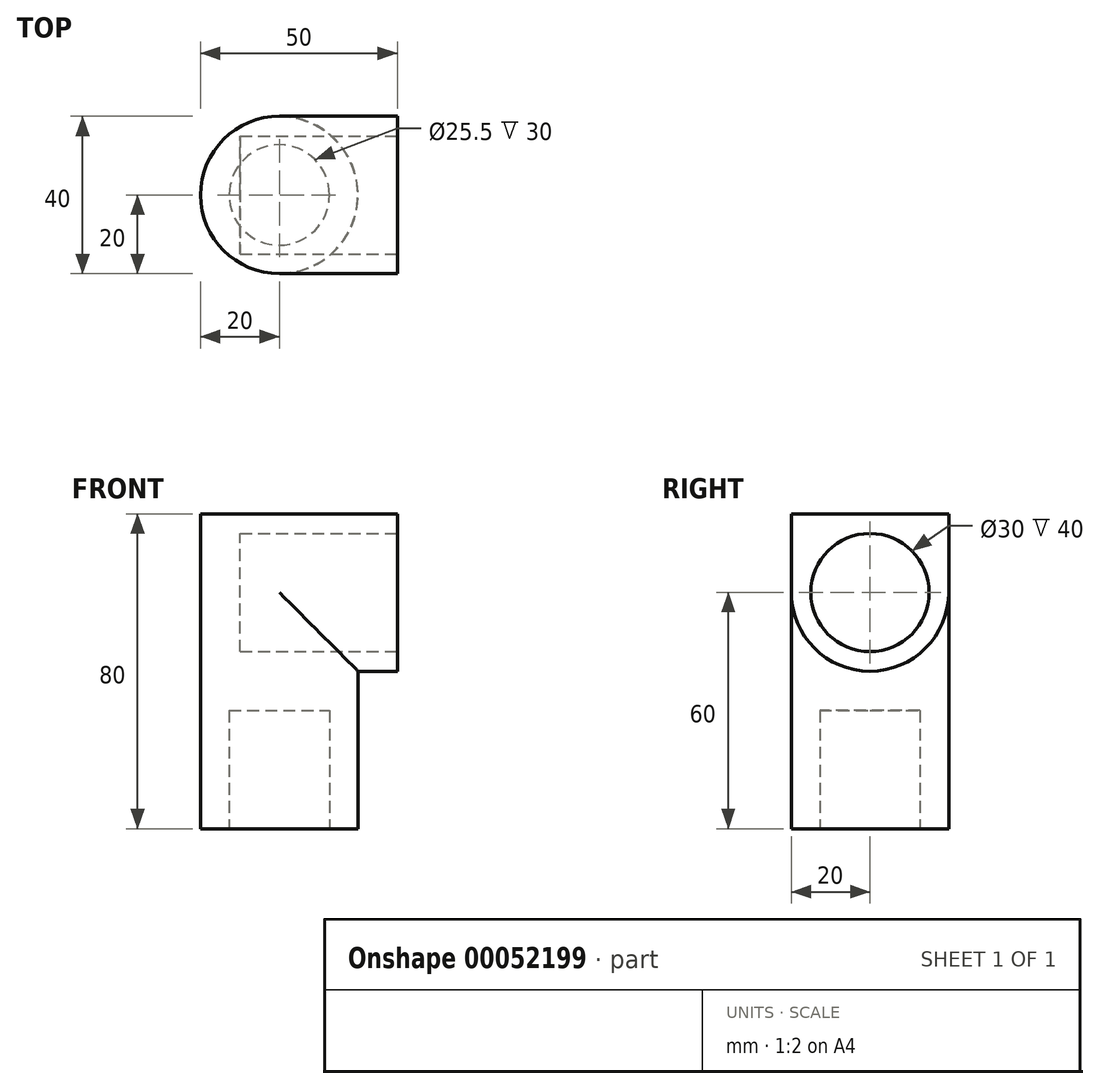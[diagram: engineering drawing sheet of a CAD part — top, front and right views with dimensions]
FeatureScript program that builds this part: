
annotation { "Feature Type Name" : "Feature", "Feature Type Description" : "" }
export const myFeature = defineFeature(function(context is Context, id is Id, definition is map)
    precondition{}
    {
        {
            var Q0;
            Q0=qCreatedBy(makeId("Front.planeOp"),FACE);
            var sketch = newSketch(context, id + "F0", { "sketchPlane" : qUnion([Q0])});
            skLineSegment(sketch, "E0", {"start": v(0, 0) * mm, "end": v(0, -40) * mm});
            skLineSegment(sketch, "E1", {"start": v(0, -40) * mm, "end": v(-40, -40) * mm});
            skLineSegment(sketch, "E2", {"start": v(-40, -40) * mm, "end": v(-40, 40) * mm});
            skLineSegment(sketch, "E3", {"start": v(-40, 40) * mm, "end": v(10, 40) * mm});
            skLineSegment(sketch, "E4", {"start": v(10, 40) * mm, "end": v(10, 0) * mm});
            skLineSegment(sketch, "E5", {"start": v(10, 0) * mm, "end": v(0, 0) * mm});
            skSolve(sketch);
        }
        {
            var Q0;
            Q0=makeQuery(id+"F0.imprint","IMPRINT",FACE,{"disambiguationData":[TD([[makeQuery(id+"F0.imprint","IMPRINT",EDGE,{"derivedFrom":sQuery(id+"F0.wireOp",EDGE,"E0")}),-1.0]])]});
            extrude(context, id + "F1", {"entities" : qUnion([Q0]), "oppositeDirection" : true, "depth" : 40 * mm});
        }
        {
            var Q0;
            Q0=makeQuery(id+"F1.opExtrude","SWEPT_FACE",FACE,{"disambiguationData":[OSD([sQuery(id+"F0.wireOp",EDGE,"E4")])]});
            var sketch = newSketch(context, id + "F2", { "sketchPlane" : qUnion([Q0])});
            skCircle(sketch, "E6", {"center": v(20, 20) * mm, "radius": 15 * mm});
            skSolve(sketch);
        }
        {
            var Q0;
            Q0 = qSketchRegion(id + "F2", true);
            extrude(context, id + "F3", {"entities" : qUnion([Q0]), "operationType" : NewBodyOperationType.REMOVE, "oppositeDirection" : true, "depth" : 40 * mm});
        }
        {
            var Q0;
            Q0=makeQuery(id+"F1.opExtrude","SWEPT_FACE",FACE,{"disambiguationData":[OSD([sQuery(id+"F0.wireOp",EDGE,"E1")])]});
            var sketch = newSketch(context, id + "F4", { "sketchPlane" : qUnion([Q0])});
            skCircle(sketch, "E7", {"center": v(-20, -20) * mm, "radius": 12.75 * mm});
            skSolve(sketch);
        }
        {
            var Q0;
            Q0=makeQuery(id+"F4.imprint","IMPRINT",FACE,{"disambiguationData":[TD([[makeQuery(id+"F4.imprint","IMPRINT",EDGE,{"derivedFrom":sQuery(id+"F4.wireOp",EDGE,"E7")}),1.0]])]});
            var Q1;
            Q1=sQuery(id+"F4.wireOp",EDGE,"E7");
            extrude(context, id + "F5", {"entities" : qUnion([Q0]), "operationType" : NewBodyOperationType.REMOVE, "surfaceEntities" : qUnion([Q1]), "oppositeDirection" : true, "depth" : 30 * mm});
        }
        {
            var Q0;
            Q0=makeQuery(id+"F1.opExtrude","CAP_EDGE",EDGE,{"disambiguationData":[OSD([sQuery(id+"F0.wireOp",EDGE,"E2")])],"isStart":false});
            var Q1;
            Q1=makeQuery(id+"F1.opExtrude","CAP_EDGE",EDGE,{"disambiguationData":[OSD([sQuery(id+"F0.wireOp",EDGE,"E2")])],"isStart":true});
            fillet(context, id + "F6", {"entities" : qUnion([Q0, Q1]), "radius" : 20 * mm, "tangentPropagation" : true, "allowEdgeOverflow" : false});
        }
        {
            var Q0;
            Q0=makeQuery(id+"F1.opExtrude","CAP_EDGE",EDGE,{"disambiguationData":[OSD([sQuery(id+"F0.wireOp",EDGE,"E0")])],"isStart":true});
            var Q1;
            Q1=makeQuery(id+"F1.opExtrude","CAP_EDGE",EDGE,{"disambiguationData":[OSD([sQuery(id+"F0.wireOp",EDGE,"E0")])],"isStart":false});
            var Q2;
            Q2=makeQuery(id+"F1.opExtrude","CAP_EDGE",EDGE,{"disambiguationData":[OSD([sQuery(id+"F0.wireOp",EDGE,"E5")])],"isStart":true});
            var Q3;
            Q3=makeQuery(id+"F1.opExtrude","CAP_EDGE",EDGE,{"disambiguationData":[OSD([sQuery(id+"F0.wireOp",EDGE,"E5")])],"isStart":false});
            fillet(context, id + "F7", {"entities" : qUnion([Q0, Q1, Q2, Q3]), "radius" : 20 * mm, "tangentPropagation" : true, "allowEdgeOverflow" : false});
        }
    });
